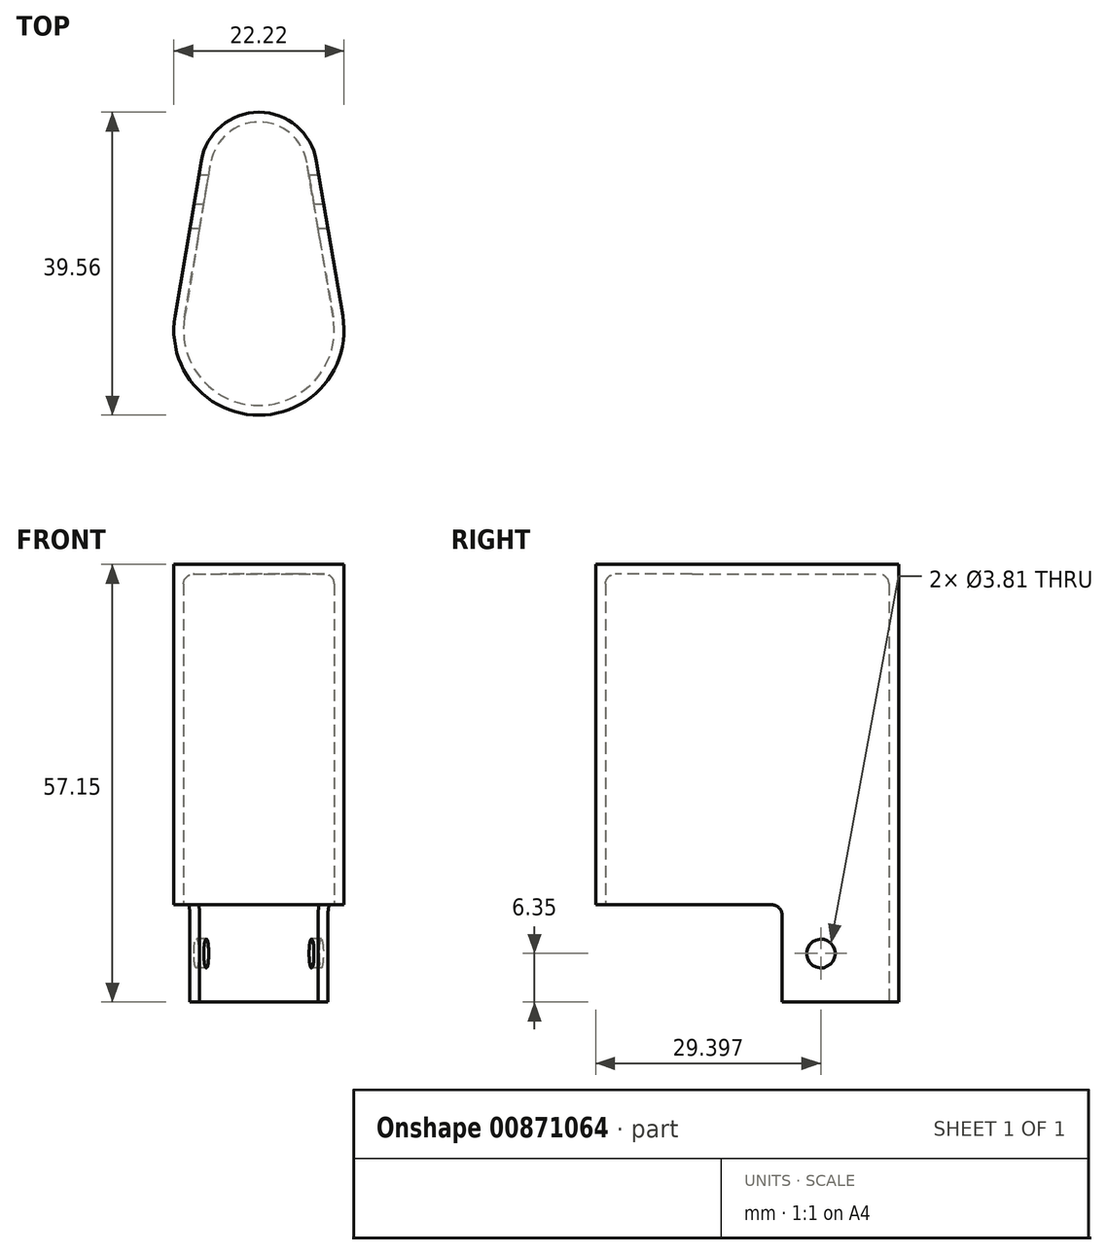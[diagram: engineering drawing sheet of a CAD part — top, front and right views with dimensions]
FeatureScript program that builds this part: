
annotation { "Feature Type Name" : "Feature", "Feature Type Description" : "" }
export const myFeature = defineFeature(function(context is Context, id is Id, definition is map)
    precondition{}
    {
        {
            var Q0;
            Q0=qCreatedBy(makeId("Top.planeOp"),FACE);
            var sketch = newSketch(context, id + "F0", { "sketchPlane" : qUnion([Q0])});
            skArc(sketch, "E0", {"start": v(2.78, 14.05) * mm, "mid": v(13.73, 1.08) * mm, "end": v(24.69, 14.05) * mm});
            skArc(sketch, "E1", {"start": v(21.24, 34.3) * mm, "mid": v(13.73, 40.64) * mm, "end": v(6.22, 34.3) * mm});
            skLineSegment(sketch, "E2", {"start": v(2.78, 14.05) * mm, "end": v(6.22, 34.3) * mm});
            skLineSegment(sketch, "E3", {"start": v(24.69, 14.05) * mm, "end": v(21.24, 34.3) * mm});
            skSolve(sketch);
        }
        {
            var Q0;
            Q0 = qSketchRegion(id + "F0", true);
            extrude(context, id + "F1", {"entities" : qUnion([Q0]), "depth" : 57.15 * mm, "offsetDistance" : 25.4 * mm});
        }
        {
            var Q0;
            Q0=makeQuery(id+"F1.opExtrude","CAP_FACE",FACE,{"disambiguationData":[OSD([sQuery(id+"F0.wireOp",EDGE,"E0"),sQuery(id+"F0.wireOp",EDGE,"E1"),sQuery(id+"F0.wireOp",EDGE,"E2"),sQuery(id+"F0.wireOp",EDGE,"E3")])],"isStart":true});
            shell(context, id + "F2", {"entities" : qUnion([Q0]), "thickness" : 1.27 * mm});
        }
        {
            var Q0;
            Q0=qCreatedBy(makeId("Right.planeOp"),FACE);
            var sketch = newSketch(context, id + "F3", { "sketchPlane" : qUnion([Q0])});
            skLineSegment(sketch, "E4.bottom", {"start": v(25.4, 12.7) * mm, "end": v(1.08, 12.7) * mm});
            skLineSegment(sketch, "E4.top", {"start": v(40.64, 0) * mm, "end": v(1.08, 0) * mm});
            skLineSegment(sketch, "E4.left", {"start": v(25.4, 12.7) * mm, "end": v(25.4, 0) * mm});
            skLineSegment(sketch, "E4.right", {"start": v(1.08, 12.7) * mm, "end": v(1.08, 0) * mm});
            skCircle(sketch, "E5", {"center": v(30.48, 6.35) * mm, "radius": 1.9 * mm});
            skSolve(sketch);
        }
        {
            var Q0;
            Q0 = qSketchRegion(id + "F3", true);
            extrude(context, id + "F4", {"entities" : qUnion([Q0]), "operationType" : NewBodyOperationType.REMOVE, "endBound" : BoundingType.THROUGH_ALL, "depth" : 25.4 * mm, "offsetDistance" : 25.4 * mm});
        }
        {
            var Q0;
            {var subQ0=sQuery(id+"F0.wireOp",EDGE,"E2");var subQ1=sQuery(id+"F3.wireOp",EDGE,"E4.bottom");var subQ2=sQuery(id+"F3.wireOp",EDGE,"E4.left");Q0=makeQuery(id+"F4.boolean.opBoolean","COPY",EDGE,{"disambiguationData":[TD([makeQuery(id+"F1.opExtrude","SWEPT_FACE",FACE,{"disambiguationData":[OSD([subQ0])]})])],"derivedFrom":makeQuery(id+"F4.opExtrude","SWEPT_EDGE",EDGE,{"disambiguationData":[OSD([subQ1,subQ2])]})});}
            var Q1;
            {var subQ0=sQuery(id+"F0.wireOp",EDGE,"E3");var subQ1=sQuery(id+"F3.wireOp",EDGE,"E4.left");var subQ2=sQuery(id+"F3.wireOp",EDGE,"E4.bottom");Q1=makeQuery(id+"F4.boolean.opBoolean","COPY",EDGE,{"disambiguationData":[TD([makeQuery(id+"F1.opExtrude","SWEPT_FACE",FACE,{"disambiguationData":[OSD([subQ0])]})])],"derivedFrom":makeQuery(id+"F4.opExtrude","SWEPT_EDGE",EDGE,{"disambiguationData":[OSD([subQ2,subQ1])]})});}
            var Q2;
            {var subQ0=sQuery(id+"F0.wireOp",EDGE,"E2");var subQ1=sQuery(id+"F3.wireOp",EDGE,"E4.left");Q2=makeQuery(id+"F4.boolean.opBoolean","COPY",EDGE,{"disambiguationData":[TD([makeQuery(id+"F1.opExtrude","SWEPT_FACE",FACE,{"disambiguationData":[OSD([subQ0])]})])],"derivedFrom":makeQuery(id+"F4.opExtrude","SWEPT_EDGE",EDGE,{"disambiguationData":[OSD([sQuery(id+"F3.wireOp",EDGE,"E4.top"),subQ1])]})});}
            var Q3;
            {var subQ0=sQuery(id+"F0.wireOp",EDGE,"E3");var subQ1=sQuery(id+"F3.wireOp",EDGE,"E4.left");Q3=makeQuery(id+"F4.boolean.opBoolean","COPY",EDGE,{"disambiguationData":[TD([makeQuery(id+"F1.opExtrude","SWEPT_FACE",FACE,{"disambiguationData":[OSD([subQ0])]})])],"derivedFrom":makeQuery(id+"F4.opExtrude","SWEPT_EDGE",EDGE,{"disambiguationData":[OSD([sQuery(id+"F3.wireOp",EDGE,"E4.top"),subQ1])]})});}
            var Q4;
            Q4=makeQuery(id+"F2.opShell","OFFSET_FACE",FACE,{"disambiguationData":[OSD([sQuery(id+"F0.wireOp",EDGE,"E0"),sQuery(id+"F0.wireOp",EDGE,"E1"),sQuery(id+"F0.wireOp",EDGE,"E2"),sQuery(id+"F0.wireOp",EDGE,"E3")])]});
            fillet(context, id + "F5", {"entities" : qUnion([Q0, Q1, Q2, Q3, Q4]), "radius" : 1.27 * mm, "tangentPropagation" : true, "allowEdgeOverflow" : false});
        }
    });
